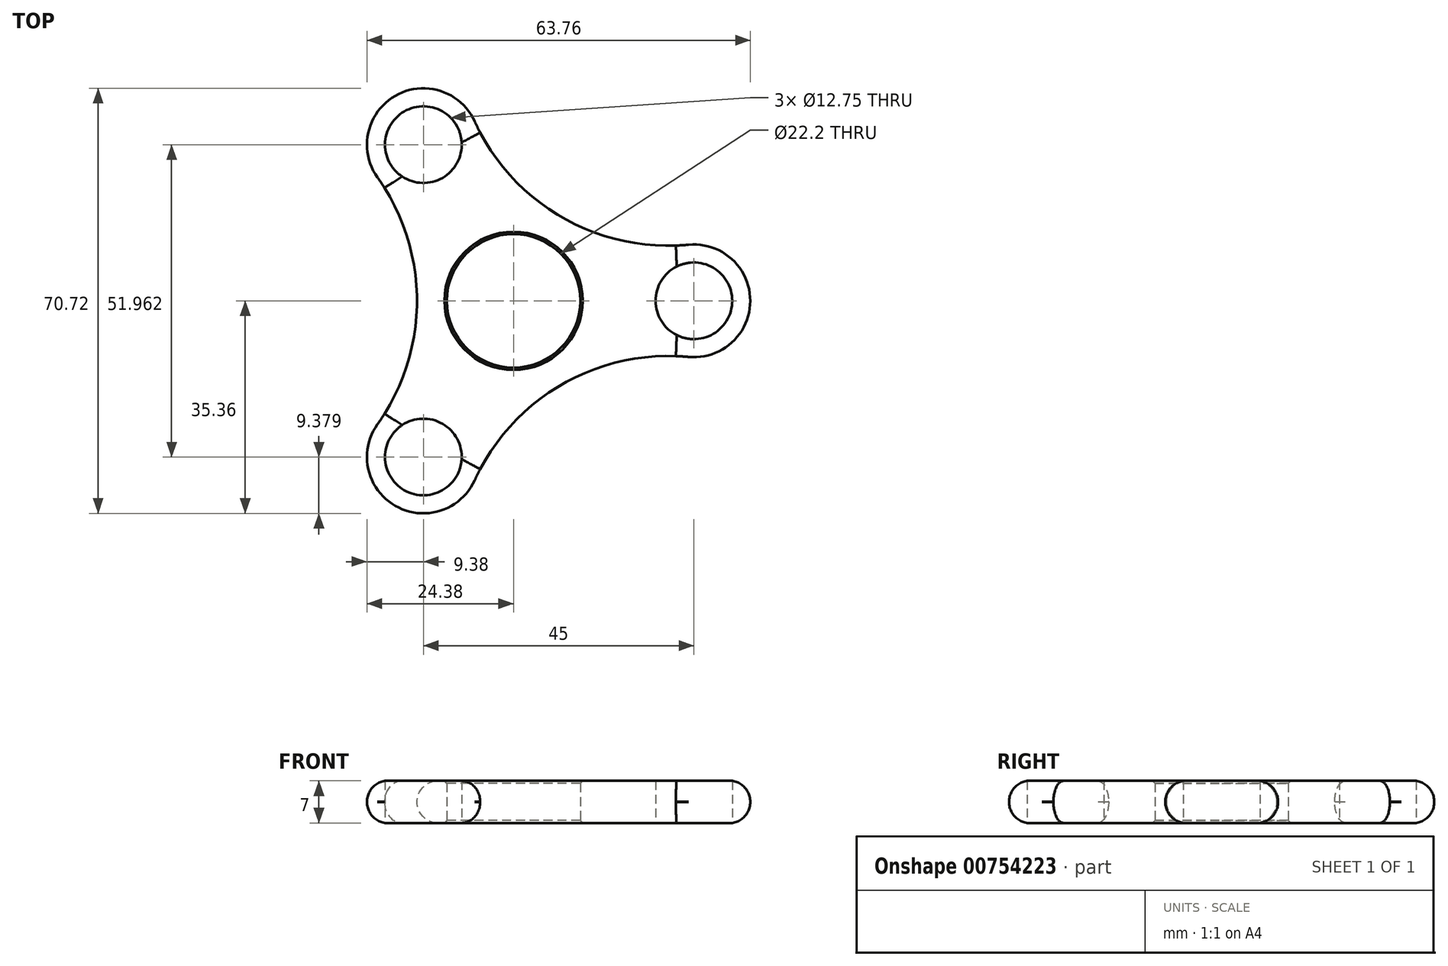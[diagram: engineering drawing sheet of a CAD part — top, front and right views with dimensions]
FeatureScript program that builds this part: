
annotation { "Feature Type Name" : "Feature", "Feature Type Description" : "" }
export const myFeature = defineFeature(function(context is Context, id is Id, definition is map)
    precondition{}
    {
        {
            var Q0;
            Q0=qCreatedBy(makeId("Top.planeOp"),FACE);
            var sketch = newSketch(context, id + "F0", { "sketchPlane" : qUnion([Q0])});
            skCircle(sketch, "E0", {"center": v(0, 0) * mm, "radius": 11.1 * mm});
            skPoint(sketch, "E1", {"position": v(30, 0) * mm});
            skCircle(sketch, "E2", {"center": v(30, 0) * mm, "radius": 6.38 * mm});
            skArc(sketch, "E3.0", {"start": v(29.1, -9.33) * mm, "mid": v(39.38, 0) * mm, "end": v(29.1, 9.33) * mm});
            skArc(sketch, "E4.1.0", {"start": v(-6.47, 29.87) * mm, "mid": v(-19.69, 34.1) * mm, "end": v(-22.63, 20.54) * mm});
            skCircle(sketch, "E4.1.1", {"center": v(-15, 25.98) * mm, "radius": 6.38 * mm});
            skArc(sketch, "E4.2.0", {"start": v(-22.63, -20.54) * mm, "mid": v(-19.69, -34.1) * mm, "end": v(-6.47, -29.87) * mm});
            skCircle(sketch, "E4.2.1", {"center": v(-15, -25.98) * mm, "radius": 6.38 * mm});
            skArc(sketch, "E5", {"start": v(29.1, -9.33) * mm, "mid": v(8.03, -13.91) * mm, "end": v(-6.47, -29.87) * mm});
            skArc(sketch, "E6.1.0", {"start": v(-6.47, 29.87) * mm, "mid": v(8.03, 13.91) * mm, "end": v(29.1, 9.33) * mm});
            skArc(sketch, "E6.2.0", {"start": v(-22.63, -20.54) * mm, "mid": v(-16.06, 0) * mm, "end": v(-22.63, 20.54) * mm});
            skSolve(sketch);
        }
        {
            var Q0;
            Q0=makeQuery(id+"F0.imprint","IMPRINT",FACE,{"disambiguationData":[TD([[makeQuery(id+"F0.imprint","IMPRINT",EDGE,{"derivedFrom":sQuery(id+"F0.wireOp",EDGE,"E4.1.1")}),-1.0]])]});
            var Q1;
            {var subQ0=sQuery(id+"F0.wireOp",EDGE,"ymMV7DUU-YaXF-13PJ-Upio-JPY2yyDOcRfn");var subQ1=sQuery(id+"F0.wireOp",EDGE,"e07e0217-3c4f-4238-9027-1b7dd3b318d3.0");var subQ2=makeQuery(id+"F0.imprint","INTERSECT",VERTEX,{"derivedFrom":[subQ1,subQ0]});Q1=makeQuery(id+"F0.imprint","IMPRINT",FACE,{"disambiguationData":[TD([[makeQuery(id+"F0.imprint","IMPRINT",EDGE,{"disambiguationData":[TD([[subQ2,1.0]])],"derivedFrom":subQ1}),-1.0]])]});}
            var Q2;
            Q2=makeQuery(id+"F0.imprint","IMPRINT",FACE,{"disambiguationData":[TD([[makeQuery(id+"F0.imprint","IMPRINT",EDGE,{"derivedFrom":sQuery(id+"F0.wireOp",EDGE,"E0")}),-1.0]])]});
            var Q3;
            {var subQ0=sQuery(id+"F0.wireOp",EDGE,"ymMV7DUU-YaXF-13PJ-Upio-JPY2yyDOcRfn");var subQ1=sQuery(id+"F0.wireOp",EDGE,"e07e0217-3c4f-4238-9027-1b7dd3b318d3.0");var subQ2=makeQuery(id+"F0.imprint","INTERSECT",VERTEX,{"derivedFrom":[subQ1,subQ0]});Q3=makeQuery(id+"F0.imprint","IMPRINT",FACE,{"disambiguationData":[TD([[makeQuery(id+"F0.imprint","IMPRINT",EDGE,{"disambiguationData":[TD([[subQ2,-1.0]])],"derivedFrom":subQ1}),-1.0]])]});}
            var Q4;
            Q4=makeQuery(id+"F0.imprint","IMPRINT",FACE,{"disambiguationData":[TD([[makeQuery(id+"F0.imprint","IMPRINT",EDGE,{"derivedFrom":sQuery(id+"F0.wireOp",EDGE,"E2")}),-1.0]])]});
            var Q5;
            {var subQ0=sQuery(id+"F0.wireOp",EDGE,"NfNrvnus-3jaq-3huT-B7Wp-5CzjeCRbWqY2");var subQ1=sQuery(id+"F0.wireOp",EDGE,"e07e0217-3c4f-4238-9027-1b7dd3b318d3.0");var subQ2=makeQuery(id+"F0.imprint","INTERSECT",VERTEX,{"derivedFrom":[subQ1,subQ0]});Q5=makeQuery(id+"F0.imprint","IMPRINT",FACE,{"disambiguationData":[TD([[makeQuery(id+"F0.imprint","IMPRINT",EDGE,{"disambiguationData":[TD([[subQ2,1.0]])],"derivedFrom":subQ1}),-1.0]])]});}
            var Q6;
            Q6=makeQuery(id+"F0.imprint","IMPRINT",FACE,{"disambiguationData":[TD([[makeQuery(id+"F0.imprint","IMPRINT",EDGE,{"derivedFrom":sQuery(id+"F0.wireOp",EDGE,"E4.2.1")}),-1.0]])]});
            extrude(context, id + "F1", {"entities" : qUnion([Q0, Q1, Q2, Q3, Q4, Q5, Q6]), "depth" : 7 * mm, "offsetDistance" : 25 * mm});
        }
        {
            var Q0;
            Q0=makeQuery(id+"F1.opExtrude","CAP_EDGE",EDGE,{"disambiguationData":[OSD([sQuery(id+"F0.wireOp",EDGE,"E5")])],"isStart":true});
            var Q1;
            Q1=makeQuery(id+"F1.opExtrude","CAP_EDGE",EDGE,{"disambiguationData":[OSD([sQuery(id+"F0.wireOp",EDGE,"E5")])],"isStart":false});
            fillet(context, id + "F2", {"entities" : qUnion([Q0, Q1]), "radius" : 3.5 * mm, "tangentPropagation" : true, "allowEdgeOverflow" : false});
        }
        {
            var Q0;
            Q0=makeQuery(id+"F1.opExtrude","CAP_EDGE",EDGE,{"disambiguationData":[OSD([sQuery(id+"F0.wireOp",EDGE,"E0")])],"isStart":false});
            var Q1;
            Q1=makeQuery(id+"F1.opExtrude","CAP_EDGE",EDGE,{"disambiguationData":[OSD([sQuery(id+"F0.wireOp",EDGE,"E0")])],"isStart":true});
            chamfer(context, id + "F3", {"entities" : qUnion([Q0, Q1]), "width" : 0.4 * mm, "tangentPropagation" : true});
        }
    });
